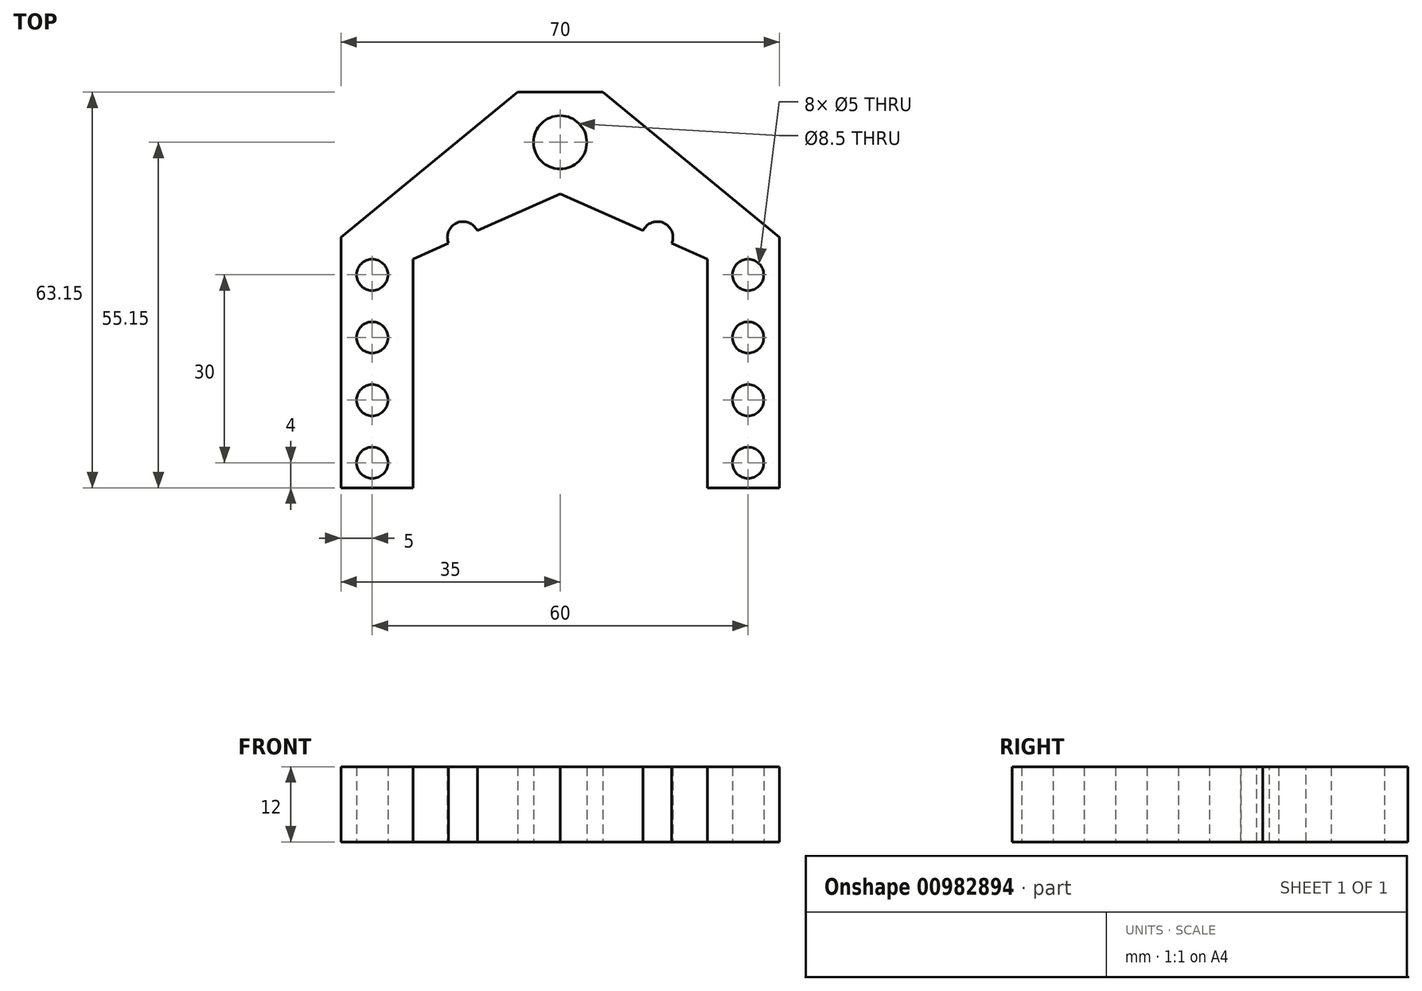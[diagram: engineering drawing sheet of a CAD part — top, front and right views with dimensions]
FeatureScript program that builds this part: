
annotation { "Feature Type Name" : "Feature", "Feature Type Description" : "" }
export const myFeature = defineFeature(function(context is Context, id is Id, definition is map)
    precondition{}
    {
        {
            var Q0;
            Q0=qCreatedBy(makeId("Top.planeOp"),FACE);
            var sketch = newSketch(context, id + "F0", { "sketchPlane" : qUnion([Q0])});
            skLineSegment(sketch, "E0.bottom", {"start": v(15.5, -15) * mm, "end": v(-15.5, -15) * mm, "construction": true});
            skLineSegment(sketch, "E0.top", {"start": v(15.5, 15) * mm, "end": v(-15.5, 15) * mm, "construction": true});
            skLineSegment(sketch, "E0.left", {"start": v(15.5, -15) * mm, "end": v(15.5, 15) * mm, "construction": true});
            skLineSegment(sketch, "E0.right", {"start": v(-15.5, -15) * mm, "end": v(-15.5, 15) * mm, "construction": true});
            skPoint(sketch, "E0.middle", {"position": v(0, 0) * mm});
            skCircle(sketch, "E1", {"center": v(-15.5, 15) * mm, "radius": 2.5 * mm});
            skCircle(sketch, "E2", {"center": v(0, 0) * mm, "radius": 12.5 * mm});
            skCircle(sketch, "E3", {"center": v(15.5, 15) * mm, "radius": 2.5 * mm});
            skCircle(sketch, "E4", {"center": v(15.5, -15) * mm, "radius": 2.5 * mm});
            skCircle(sketch, "E5", {"center": v(-15.5, -15) * mm, "radius": 2.5 * mm});
            skLineSegment(sketch, "E6", {"start": v(-35, 38.15) * mm, "end": v(-35, -25) * mm});
            skLineSegment(sketch, "E7", {"start": v(-35, -25) * mm, "end": v(35, -25) * mm});
            skLineSegment(sketch, "E8", {"start": v(35, -25) * mm, "end": v(35, 38.15) * mm});
            skLineSegment(sketch, "E9", {"start": v(35, 38.15) * mm, "end": v(-35, 38.15) * mm});
            skLineSegment(sketch, "E10", {"start": v(-35, 30.15) * mm, "end": v(35, 30.15) * mm, "construction": true});
            skCircle(sketch, "E11", {"center": v(0, 30.15) * mm, "radius": 4.25 * mm});
            skLineSegment(sketch, "E12.bottom", {"start": v(22, -22) * mm, "end": v(-22, -22) * mm, "construction": true});
            skLineSegment(sketch, "E12.top", {"start": v(22, 22) * mm, "end": v(-22, 22) * mm, "construction": true});
            skLineSegment(sketch, "E12.left", {"start": v(22, -22) * mm, "end": v(22, 22) * mm, "construction": true});
            skLineSegment(sketch, "E12.right", {"start": v(-22, -22) * mm, "end": v(-22, 22) * mm, "construction": true});
            skLineSegment(sketch, "E13", {"start": v(30, 38.15) * mm, "end": v(30, -25) * mm, "construction": true});
            skCircle(sketch, "E14", {"center": v(30, -21) * mm, "radius": 2.5 * mm});
            skCircle(sketch, "E15", {"center": v(30, -11) * mm, "radius": 2.5 * mm});
            skCircle(sketch, "E16", {"center": v(30, -1) * mm, "radius": 2.5 * mm});
            skCircle(sketch, "E17", {"center": v(30, 9) * mm, "radius": 2.5 * mm});
            skCircle(sketch, "E18.MirrorC", {"center": v(-30, 9) * mm, "radius": 2.5 * mm});
            skCircle(sketch, "E19.MirrorC", {"center": v(-30, -1) * mm, "radius": 2.5 * mm});
            skCircle(sketch, "E20.MirrorC", {"center": v(-30, -11) * mm, "radius": 2.5 * mm});
            skCircle(sketch, "E21.MirrorC", {"center": v(-30, -21) * mm, "radius": 2.5 * mm});
            skLineSegment(sketch, "E22", {"start": v(-35, 15.02) * mm, "end": v(-6.81, 38.15) * mm});
            skLineSegment(sketch, "E23.MirrorCS", {"start": v(35, 15.02) * mm, "end": v(6.81, 38.15) * mm});
            skSolve(sketch);
        }
        {
            var Q0;
            Q0=makeQuery(id+"F0.imprint","IMPRINT",FACE,{"disambiguationData":[TD([[makeQuery(id+"F0.imprint","IMPRINT",EDGE,{"derivedFrom":sQuery(id+"F0.wireOp",EDGE,"E1")}),-1.0]])]});
            extrude(context, id + "F1", {"entities" : qUnion([Q0]), "depth" : 12 * mm, "offsetDistance" : 25 * mm});
        }
        {
            var Q0;
            Q0=makeQuery(id+"F1.opExtrude","CAP_FACE",FACE,{"disambiguationData":[OSD([sQuery(id+"F0.wireOp",EDGE,"E1"),sQuery(id+"F0.wireOp",EDGE,"E2"),sQuery(id+"F0.wireOp",EDGE,"E3"),sQuery(id+"F0.wireOp",EDGE,"E4"),sQuery(id+"F0.wireOp",EDGE,"E5"),sQuery(id+"F0.wireOp",EDGE,"E6"),sQuery(id+"F0.wireOp",EDGE,"E7"),sQuery(id+"F0.wireOp",EDGE,"E8"),sQuery(id+"F0.wireOp",EDGE,"E9"),sQuery(id+"F0.wireOp",EDGE,"E11"),sQuery(id+"F0.wireOp",EDGE,"E14"),sQuery(id+"F0.wireOp",EDGE,"E15"),sQuery(id+"F0.wireOp",EDGE,"E16"),sQuery(id+"F0.wireOp",EDGE,"E17"),sQuery(id+"F0.wireOp",EDGE,"E18.MirrorC"),sQuery(id+"F0.wireOp",EDGE,"E19.MirrorC"),sQuery(id+"F0.wireOp",EDGE,"E20.MirrorC"),sQuery(id+"F0.wireOp",EDGE,"E21.MirrorC"),sQuery(id+"F0.wireOp",EDGE,"E22"),sQuery(id+"F0.wireOp",EDGE,"E23.MirrorCS")])],"isStart":false});
            var sketch = newSketch(context, id + "F2", { "sketchPlane" : qUnion([Q0])});
            skLineSegment(sketch, "E24", {"start": v(-23.5, -25) * mm, "end": v(-23.5, 11.5) * mm});
            skLineSegment(sketch, "E25", {"start": v(-23.5, 11.5) * mm, "end": v(0, 21.9) * mm});
            skLineSegment(sketch, "E26.MirrorCS", {"start": v(23.5, -25) * mm, "end": v(23.5, 11.5) * mm});
            skLineSegment(sketch, "E27.MirrorCS", {"start": v(23.5, 11.5) * mm, "end": v(0, 21.9) * mm});
            skSolve(sketch);
        }
        {
            var Q0;
            {var subQ6=sQuery(id+"F2.wireOp",EDGE,"E24");Q0=makeQuery(id+"F2.imprint","IMPRINT",FACE,{"disambiguationData":[TD([[makeQuery(id+"F2.imprint","IMPRINT",EDGE,{"derivedFrom":subQ6}),-1.0]])]});}
            extrude(context, id + "F3", {"entities" : qUnion([Q0]), "operationType" : NewBodyOperationType.REMOVE, "oppositeDirection" : true, "depth" : 25 * mm, "offsetDistance" : 25 * mm});
        }
    });
